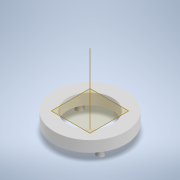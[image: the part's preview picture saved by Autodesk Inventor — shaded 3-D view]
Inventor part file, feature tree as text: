
AUTODESK INVENTOR PART (.ipt)
format: ipt  version: 2021 (Build 250183000, 183)  size: 338,432 bytes
history: native  units: in
note: dims shown in document units (in); Inventor stores cm internally (conversion verified against a paired STEP export)
features: sketch x7, extrude x6, other x1, revolve x1, pattern_circular x1, mirror x1, fillet x1, plane x1
ambient origin geometry x8: Origin, YZ Plane, XZ Plane, XY Plane, X Axis, Y Axis, Z Axis, Center Point
bodies: Solid1 (feature_tree)
feature tree (19):
  extrude  "Extrusion1"  Depth=1.0236in
  other  "Work Axis1"
  revolve  "Revolution1"  [1 undecoded]
  extrude  "Extrusion2"  Depth=1.0079in
  extrude  "Extrusion3"  TaperAngle=90.0deg  [1 undecoded]
  extrude  "Extrusion4"  Depth=0.8976in
  extrude  "Extrusion5"  Depth=1.0236in TaperAngle=0.0deg
  pattern_circular  "Circular Pattern1"  [2 undecoded]
  mirror  "Mirror1"
  fillet  "Fillet2"  Radius=0.8268in
  plane  "Work Plane1"
  extrude  "Extrusion7"  Depth=0.1969in TaperAngle=0.0deg
  sketch  "Sketch1"  dims[d0=2.0472in d1=1.0236in]
  sketch  "Sketch2"  dims[d2=1.0236in d3=1.0236in]
  sketch  "Sketch3"  dims[d4=1.378in d5=0.0in d6=1.0079in]
  sketch  "Sketch4"  dims[d7=90.0deg d8=90.0deg]
  sketch  "Sketch5"  dims[d9=0.0394in d10=0.0in d11=0.8976in]
  sketch  "Sketch8"  dims[d12=0.0in d13=0.0in d14=1.0236in d15=0.0in]
  sketch  "Sketch10"  dims[d16=1.2913in d21=0.2126in d22=0.8268in d23=0.1969in d24=0.0in d25=1.9685in d26=240.0deg d33=0.5039in d34=0.0394in d35=-1.0236in d36=1.5748in d37=0.0in]
note: 4 required parameter values undecoded (feature->parameter linkage not recoverable at this tier; creation-order binding heuristic only, values carry confidence <= 0.55)